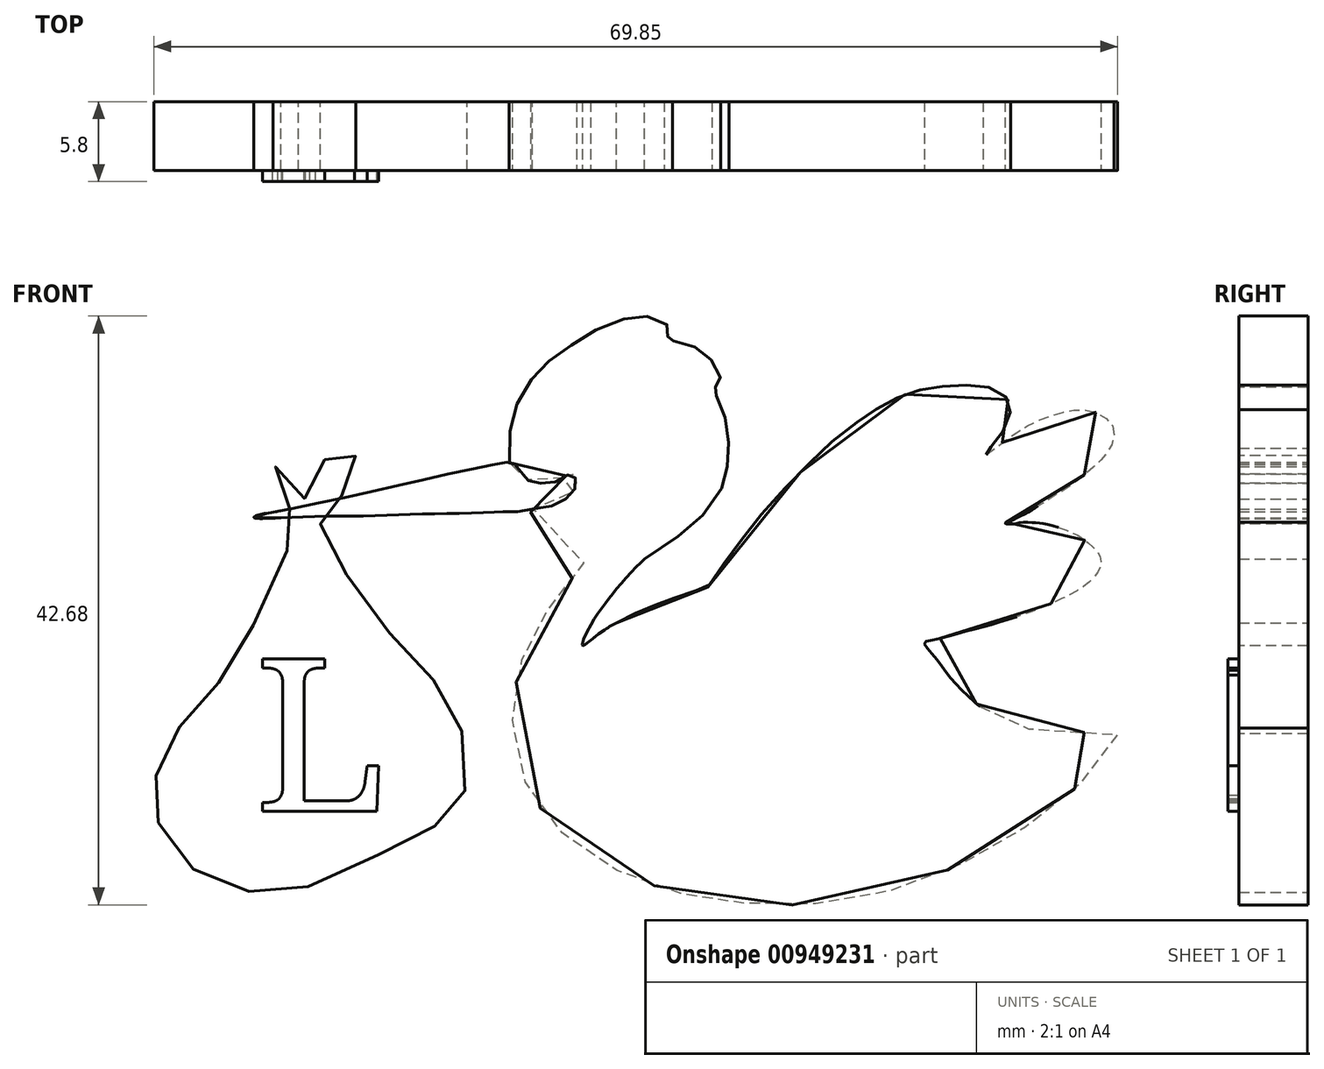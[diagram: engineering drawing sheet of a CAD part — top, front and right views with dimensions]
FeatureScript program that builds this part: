
annotation { "Feature Type Name" : "Feature", "Feature Type Description" : "" }
export const myFeature = defineFeature(function(context is Context, id is Id, definition is map)
    precondition{}
    {
        {
            var Q0;
            Q0=qCreatedBy(makeId("Front.planeOp"),FACE);
            var sketch = newSketch(context, id + "F0", { "sketchPlane" : qUnion([Q0])});
            skFitSpline(sketch, "E0", {"points": [v(-11.5, 15.4) * mm, v(-11.52, 17.2) * mm, v(-11.29, 18.61) * mm, v(-10.87, 19.85) * mm, v(-10.16, 21.07) * mm, v(-9.27, 22.18) * mm, v(-8.56, 22.82) * mm, v(-7.52, 23.55) * mm, v(-6.41, 24.3) * mm, v(-5.08, 25.08) * mm, v(-3.56, 25.7) * mm, v(-2.51, 25.98) * mm, v(-1.57, 25.98) * mm, v(-0.74, 25.76) * mm, v(-0.1, 25.4) * mm, v(0.3, 25.06) * mm, v(0.23, 24.74) * mm, v(-0.22, 24.4) * mm, v(-0.3, 24.3) * mm, v(-0.11, 24.26) * mm, v(0.55, 24.2) * mm, v(1.37, 23.99) * mm, v(2.18, 23.64) * mm, v(2.74, 23.27) * mm, v(3.3, 22.62) * mm, v(3.65, 22) * mm, v(3.8, 21.45) * mm, v(3.78, 21.02) * mm, v(3.71, 20.88) * mm, v(3.39, 20.86) * mm, v(3.22, 20.92) * mm, v(3.17, 20.85) * mm, v(3.34, 20.52) * mm, v(3.75, 19.68) * mm, v(4.07, 18.85) * mm, v(4.31, 17.68) * mm, v(4.4, 16.65) * mm, v(4.37, 15.67) * mm, v(4.22, 14.67) * mm, v(4.01, 13.9) * mm, v(3.46, 12.75) * mm, v(2, 11.09) * mm, v(0.67, 10.02) * mm, v(-1.7, 8.41) * mm], "startDerivative": vector(-2.35, 56.4) * mm, "endDerivative": vector(-37.56, -42.45) * mm});
            skFitSpline(sketch, "E1", {"points": [v(-1.7, 8.41) * mm, v(-2.49, 7.65) * mm, v(-3.62, 6.37) * mm, v(-4.31, 5.5) * mm, v(-5.06, 4.5) * mm, v(-5.75, 3.36) * mm, v(-6.23, 2.14) * mm, v(-6.04, 2.18) * mm, v(-5, 3) * mm, v(-3.75, 3.78) * mm], "startDerivative": vector(-7.05, -6.59) * mm, "endDerivative": vector(9.85, 5.13) * mm});
            skFitSpline(sketch, "E2", {"points": [v(-3.75, 3.78) * mm, v(-2.95, 4.2) * mm, v(-2, 4.64) * mm, v(-1.06, 5.02) * mm, v(-0.46, 5.24) * mm, v(0.54, 5.6) * mm, v(1.66, 6) * mm, v(2.43, 6.22) * mm, v(2.82, 6.32) * mm, v(3.1, 6.76) * mm, v(4, 8) * mm, v(5.07, 9.45) * mm, v(6.4, 11.2) * mm, v(8.1, 13.13) * mm, v(10, 15.1) * mm, v(11.36, 16.45) * mm, v(13.25, 17.99) * mm, v(14.21, 18.66) * mm, v(15.27, 19.37) * mm, v(16.39, 19.97) * mm, v(17.31, 20.38) * mm, v(18.68, 20.75) * mm, v(19.66, 20.88) * mm, v(20.76, 20.97) * mm, v(22.14, 20.99) * mm, v(23.1, 20.87) * mm, v(23.98, 20.54) * mm, v(24.52, 20.1) * mm, v(24.77, 19.58) * mm, v(24.8, 18.99) * mm, v(24.57, 18.28) * mm, v(24.02, 17.3) * mm, v(23.57, 16.71) * mm, v(23.07, 16.17) * mm, v(22.83, 15.89) * mm, v(23.19, 16.04) * mm, v(23.83, 16.53) * mm, v(24.73, 17.2) * mm, v(25.58, 17.78) * mm, v(26.58, 18.31) * mm, v(27.6, 18.75) * mm, v(28.47, 19) * mm, v(29.16, 19.16) * mm, v(29.94, 19.22) * mm, v(30.76, 19.12) * mm, v(31.5, 18.77) * mm, v(32.03, 18.31) * mm, v(32.3, 17.86) * mm, v(32.3, 17.3) * mm, v(32.16, 16.71) * mm, v(31.96, 16.36) * mm, v(31.65, 15.9) * mm, v(31.2, 15.4) * mm, v(30.7, 14.95) * mm, v(30.08, 14.43) * mm, v(29.54, 13.99) * mm, v(28.92, 13.56) * mm, v(28.2, 13.11) * mm, v(27.49, 12.65) * mm, v(26.77, 12.21) * mm, v(26.3, 11.91) * mm, v(25.6, 11.54) * mm, v(24.97, 11.23) * mm, v(24.41, 10.98) * mm, v(24.82, 10.93) * mm, v(25.15, 10.96) * mm, v(25.64, 11.06) * mm, v(26.37, 11.05) * mm, v(26.94, 11) * mm, v(27.68, 10.87) * mm, v(28.92, 10.47) * mm, v(29.49, 10.22) * mm, v(30.16, 9.8) * mm, v(30.76, 9.3) * mm, v(31.2, 8.81) * mm, v(31.37, 8.28) * mm, v(31.32, 7.79) * mm, v(30.9, 7.13) * mm, v(30.33, 6.58) * mm, v(29.37, 5.95) * mm, v(28.23, 5.39) * mm, v(27.1, 4.88) * mm, v(26.04, 4.48) * mm, v(24.8, 4.07) * mm, v(23.57, 3.7) * mm, v(22.44, 3.38) * mm, v(21.08, 3.03) * mm, v(19.93, 2.7) * mm, v(18.92, 2.49) * mm, v(18.58, 2.36) * mm, v(18.65, 2.14) * mm, v(19.07, 1.6) * mm, v(19.73, 0.77) * mm, v(20.3, 0) * mm, v(20.92, -0.71) * mm, v(21.8, -1.6) * mm, v(22.58, -2.28) * mm, v(23.45, -2.8) * mm, v(24.58, -3.44) * mm, v(25.7, -3.81) * mm, v(26.84, -4.06) * mm, v(28.1, -4.24) * mm, v(29.38, -4.24) * mm, v(30.59, -4.13) * mm, v(31.5, -4.02) * mm, v(32.1, -3.88) * mm, v(32.43, -3.9) * mm, v(32.56, -4.15) * mm, v(32.52, -4.55) * mm, v(31.63, -5.95) * mm, v(30.5, -7.28) * mm, v(29.14, -8.54) * mm, v(27.6, -9.85) * mm, v(26, -10.98) * mm, v(24.2, -12.14) * mm, v(22.34, -13.18) * mm, v(20.22, -14.17) * mm, v(17.97, -15.08) * mm, v(15.65, -15.77) * mm, v(13.95, -16.15) * mm, v(11.26, -16.55) * mm, v(8.76, -16.67) * mm, v(6.75, -16.64) * mm, v(4.96, -16.5) * mm, v(3.24, -16.27) * mm, v(2, -16.1) * mm, v(0.12, -15.64) * mm, v(-1.85, -14.98) * mm, v(-3.51, -14.3) * mm, v(-5.11, -13.37) * mm, v(-6.6, -12.37) * mm, v(-7.92, -11.24) * mm, v(-9.06, -9.95) * mm, v(-9.97, -8.5) * mm, v(-10.55, -7.32) * mm, v(-11.09, -5.46) * mm, v(-11.28, -4.03) * mm, v(-11.25, -2.39) * mm, v(-11.08, -0.78) * mm, v(-10.75, 0.58) * mm, v(-10.26, 1.99) * mm, v(-9.54, 3.37) * mm, v(-9.07, 4.16) * mm, v(-8.58, 4.9) * mm, v(-7.81, 5.84) * mm, v(-6.75, 7.27) * mm, v(-5.86, 8.39) * mm, v(-5.64, 8.76) * mm, v(-6.03, 9.01) * mm, v(-6.74, 9.26) * mm, v(-7.76, 9.84) * mm, v(-8.86, 10.68) * mm, v(-9.62, 11.43) * mm, v(-9.98, 11.85) * mm, v(-9.83, 12.01) * mm, v(-8.74, 12.16) * mm, v(-7.92, 12.44) * mm, v(-7.4, 12.78) * mm, v(-6.92, 13.23) * mm, v(-6.72, 13.57) * mm, v(-6.65, 14) * mm, v(-6.72, 14.29) * mm, v(-6.87, 14.5) * mm, v(-7.12, 14.56) * mm, v(-7.45, 14.4) * mm, v(-8.01, 14.08) * mm, v(-8.58, 13.9) * mm, v(-9.2, 13.88) * mm, v(-9.8, 13.95) * mm, v(-10.13, 14.1) * mm, v(-10.49, 14.33) * mm, v(-10.64, 14.65) * mm, v(-10.73, 14.9) * mm, v(-10.91, 15.15) * mm, v(-11.19, 15.26) * mm, v(-11.4, 15.29) * mm, v(-11.5, 15.4) * mm], "startDerivative": vector(142.2, 79.35) * mm, "endDerivative": vector(-37.4, 61.03) * mm});
            skSolve(sketch);
        }
        {
            var Q0;
            Q0=qCreatedBy(makeId("Front.planeOp"),FACE);
            var sketch = newSketch(context, id + "F1", { "sketchPlane" : qUnion([Q0])});
            skFitSpline(sketch, "E3", {"points": [v(-9.83, 12.01) * mm, v(-8.74, 12.16) * mm, v(-7.92, 12.44) * mm, v(-7.4, 12.78) * mm, v(-6.92, 13.23) * mm, v(-6.72, 13.57) * mm, v(-6.65, 14) * mm, v(-6.72, 14.29) * mm, v(-6.87, 14.5) * mm, v(-7.12, 14.56) * mm, v(-7.45, 14.4) * mm, v(-8.01, 14.08) * mm, v(-8.58, 13.9) * mm, v(-9.2, 13.88) * mm, v(-9.8, 13.95) * mm, v(-10.13, 14.1) * mm, v(-10.49, 14.33) * mm, v(-10.64, 14.65) * mm, v(-10.73, 14.9) * mm, v(-10.91, 15.15) * mm, v(-11.19, 15.26) * mm, v(-11.4, 15.29) * mm, v(-11.5, 15.4) * mm, v(-11.94, 15.35) * mm, v(-12.5, 15.26) * mm, v(-13.51, 15.05) * mm, v(-15.16, 14.73) * mm, v(-16.73, 14.4) * mm, v(-18.56, 13.95) * mm, v(-20.56, 13.5) * mm, v(-22.82, 12.98) * mm, v(-24.8, 12.57) * mm, v(-26.8, 12.16) * mm, v(-28.88, 11.75) * mm, v(-29.78, 11.57) * mm, v(-30.03, 11.41) * mm, v(-28.08, 11.38) * mm], "startDerivative": vector(34.14, 3.27) * mm, "endDerivative": vector(85.62, 3.73) * mm});
            skFitSpline(sketch, "E4", {"points": [v(-28.08, 11.38) * mm, v(-25.59, 11.5) * mm, v(-22.64, 11.52) * mm, v(-19.9, 11.58) * mm, v(-17.1, 11.68) * mm, v(-14.1, 11.73) * mm, v(-11.95, 11.82) * mm, v(-10.98, 11.84) * mm, v(-9.83, 12.01) * mm], "startDerivative": vector(18.29, 1.02) * mm, "endDerivative": vector(13.2, 2.43) * mm});
            skSolve(sketch);
        }
        {
            var Q0;
            Q0=qCreatedBy(makeId("Front.planeOp"),FACE);
            var sketch = newSketch(context, id + "F2", { "sketchPlane" : qUnion([Q0])});
            skFitSpline(sketch, "E5", {"points": [v(-27.44, 12.06) * mm, v(-28.01, 12.8) * mm, v(-28.42, 13.64) * mm, v(-28.6, 14.4) * mm, v(-28.57, 14.98) * mm, v(-28.3, 15.1) * mm, v(-27.9, 14.94) * mm, v(-27.42, 14.56) * mm, v(-26.74, 13.63) * mm, v(-26.4, 12.85) * mm, v(-26.32, 12.75) * mm, v(-26.22, 13.29) * mm, v(-25.94, 14.01) * mm, v(-25.52, 14.78) * mm, v(-24.91, 15.58) * mm, v(-24.3, 16.11) * mm, v(-23.64, 16.4) * mm, v(-23.17, 16.42) * mm, v(-22.89, 16.3) * mm, v(-22.71, 16.06) * mm, v(-22.64, 15.6) * mm, v(-22.73, 14.87) * mm, v(-22.96, 14.23) * mm, v(-23.23, 13.63) * mm, v(-23.55, 13.1) * mm, v(-23.8, 12.82) * mm, v(-24.1, 12.45) * mm, v(-24.4, 12.15) * mm, v(-24.73, 11.92) * mm, v(-25, 11.76) * mm, v(-25.2, 10.96) * mm, v(-24.97, 10.4) * mm, v(-24.44, 9.26) * mm, v(-23.72, 7.96) * mm, v(-23.03, 6.85) * mm, v(-22.2, 5.61) * mm, v(-21.1, 4.12) * mm, v(-19.3, 2.05) * mm, v(-18.37, 1.04) * mm, v(-17.51, 0.18) * mm, v(-16.85, -0.59) * mm, v(-16.15, -1.51) * mm, v(-15.63, -2.54) * mm, v(-15.04, -3.83) * mm, v(-14.7, -5.12) * mm, v(-14.57, -6.3) * mm, v(-14.6, -7.73) * mm, v(-14.9, -8.94) * mm, v(-15.63, -10.32) * mm, v(-16.15, -10.81) * mm, v(-16.4, -10.9) * mm, v(-16.96, -10.98) * mm, v(-17.65, -11.21) * mm, v(-18.94, -11.87) * mm, v(-20.56, -12.78) * mm, v(-22.1, -13.68) * mm, v(-24.1, -14.64) * mm, v(-26.22, -15.4) * mm, v(-27.74, -15.7) * mm, v(-29.12, -15.74) * mm, v(-29.97, -15.74) * mm, v(-31.4, -15.5) * mm, v(-32.77, -15) * mm, v(-33.71, -14.55) * mm, v(-34.65, -13.91) * mm, v(-35.58, -13.06) * mm, v(-36.37, -12) * mm, v(-36.88, -10.9) * mm, v(-37.17, -9.91) * mm, v(-37.25, -9.33) * mm, v(-37.28, -8.47) * mm, v(-37.2, -7.71) * mm, v(-37.02, -6.82) * mm, v(-36.74, -6) * mm, v(-36.34, -5.16) * mm, v(-35.67, -4.11) * mm, v(-34.8, -2.98) * mm, v(-34.12, -2.25) * mm, v(-33.13, -1.1) * mm, v(-32.38, -0.33) * mm, v(-31.66, 0.84) * mm, v(-30.65, 2.53) * mm, v(-29.85, 4.09) * mm, v(-28.68, 6.56) * mm, v(-27.82, 8.55) * mm, v(-27.09, 10.28) * mm, v(-26.8, 10.87) * mm, v(-27.04, 11.43) * mm, v(-27.29, 11.83) * mm, v(-27.44, 12.06) * mm]});
            skSolve(sketch);
        }
        {
            var Q0;
            Q0 = qSketchRegion(id + "F0", true);
            var Q1;
            Q1 = qSketchRegion(id + "F1", true);
            var Q2;
            Q2 = qSketchRegion(id + "F2", true);
            extrude(context, id + "F3", {"entities" : qUnion([Q0, Q1, Q2]), "depth" : 5 * mm, "offsetDistance" : 25 * mm});
        }
        {
            var Q0;
            Q0=makeQuery(id+"F3.opExtrude","CAP_FACE",FACE,{"disambiguationData":[OSD([sQuery(id+"F2.wireOp",EDGE,"E5")])],"isStart":false});
            cPlane(context, id + "F4", {"entities" : qUnion([Q0]), "cplaneType" : CPlaneType.OFFSET, "offset" : 0 * mm, "width" : 150 * mm, "height" : 150 * mm});
        }
        {
            var Q0;
            Q0=qCreatedBy(id+"F4.planeOp",FACE);
            var sketch = newSketch(context, id + "F5", { "sketchPlane" : qUnion([Q0])});
            skText(sketch, "E6", { "text": "L", "fontName": "NotoSerif-Regular.ttf"});
            const initialGuessF5  = {"E6": [-0.03, -0.0099, 1, 0, 0.01115]};
            skSetInitialGuess(sketch, initialGuessF5);
            skSolve(sketch);
        }
        {
            var Q0;
            Q0 = qSketchRegion(id + "F5", true);
            extrude(context, id + "F6", {"entities" : qUnion([Q0]), "operationType" : NewBodyOperationType.ADD, "depth" : 0.8 * mm, "offsetDistance" : 25 * mm});
        }
    });
